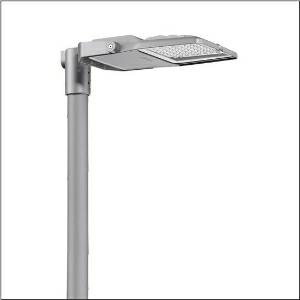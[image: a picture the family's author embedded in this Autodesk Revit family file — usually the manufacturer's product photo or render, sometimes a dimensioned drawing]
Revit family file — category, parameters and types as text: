
# Revit family: floodlight_fl_21_iq_mini___pl61_5xa7771b2c3a_a4a3
name_source: partatom
category: Lighting Fixtures
units: mm (PartAtom-declared; Revit-internal decimal feet)

## family parameters
Cut with Voids When Loaded = No
Host = Face
Light Source = No
Part Type = Normal
Room Calculation Point = No
Round Connector Dimension = Use Diameter
Shared = No

## types (1)
- --- (1 x LED, 6120 lm, 45.5 W, 3000K)
    Apparent Load = 46 VA
    CIE Flux Codes = 33 65 98 100 100
    Color Rendering = 70
    Color Temperature = 3000K
    Default Elevation = 1800 mm
    Description = Floodlight FL 21 iQ mini, floodlight, primary light control with lens, of PMMA, primary optical cover: protective disc, of toughened safety glass, transparent, light distribution: PL61, light emission: direct distribution, installation type: surface-mounted, LED, High Power LED, rated luminous flux: 6.120lm, luminous efficacy: 135lm/W, light colour: 730, colour temperature: 3000K, control gear: iQ Comfort/DALI, control: Auto-Match, Temp-Guard, Lumen-Switch, Night-Set, Smart-Wire, Light-Fading, Desk-Remote (wireless, voltage-free reading and setting of iQ features in the workshop via application-optimized NFC function/RFID function), optimised constant luminous flux control (CLO 2.0), with terminal, 6-pole, mains connection: 220..240V, AC, 50/60Hz, start of lifetime: 46W, end of service life: 48W, reduction: 22W, luminaire housing, of diecast aluminium, powder-coated, Siteco® metallic grey (DB 702S), corrosivity category C5 mid according to DIN EN ISO 12944, suitable for swimming pools, chlorine-resistant, sealing non-destructively replaceable, please order mast flange separately, mast bracket, of steel, galvanised, powder-coated, Siteco® metallic grey (DB 702S), protection rating (complete): IP66, insulation class (complete): insulation class II (safety insulation), certification: CE, ENEC, VDE, protection symbol: D, impact resistance: IK08, permissible operating ambient temperature: -40..+40°C, permissible operating ambient temperature for outdoor applications: -40..+50°C, standard: DIN EN 12944, LABS conformity tested according to VDMA 24364:2018-05, packaging unit: 1 piece

Light Distribution: PL61
    Height = 70 mm
    Lamp = 1 x LED
    Lamp Light Flux = 6120 lm
    Lamp Power = 45.5 W
    Lamp count = 1
    Length = 485 mm
    Luminous efficacy = 135 lm/W
    Manufacturer = Siteco
    ModVariant = No
    Model = 5XA7771B2C3A
    Number of Poles = 1
    OnlyDefault = Yes
    Power Factor = 1
    Product Name = Floodlight FL 21 iQ mini | PL61
    Product group = floodlight | pylon annexe
    ProductGroupID = 6200
    Protection Class = Protection class II
    Protection Degree = IP 66
    RLX_Detail_Level = 1
    RLX_Emergency_Light_Flux = 0 lm
    RLX_Emergency_Type = 0
    RLX_Emergency_Type_DB = No
    RlxData = <blob elided: 101521 chars, md5=70d40da7>
    Socket = socket
    Standby Power = 0 W
    System Light Flux = 6120 lm
    System Power = 46 W
    Type Comments = factory setting: luminous flux: 100 % | dim-lin: 254 | 463 mA
    Type Image = l_1007125.jpg
    URL = http://relux.com
    VarID = @adj_173836
    Voltage = 0 V
    Weight = 0.00 kg
    Width = 337 mm

## geometry (parser evidence)
native form markers: Blend x4, Sweep x11
no freeform markers — native parametric forms only
